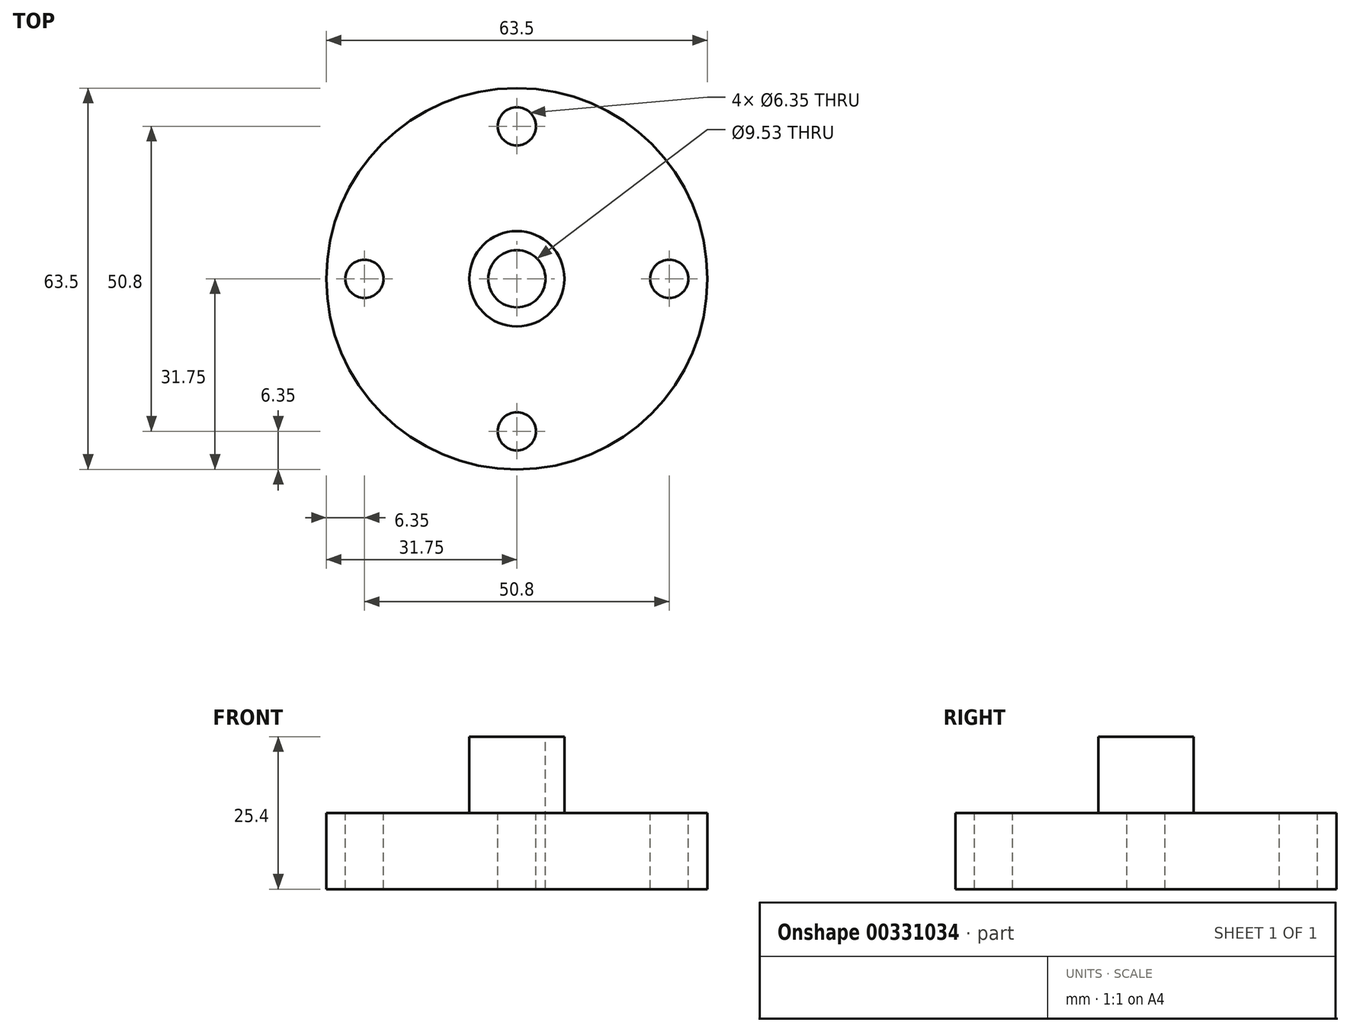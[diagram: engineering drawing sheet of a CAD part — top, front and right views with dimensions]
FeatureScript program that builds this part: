
annotation { "Feature Type Name" : "Feature", "Feature Type Description" : "" }
export const myFeature = defineFeature(function(context is Context, id is Id, definition is map)
    precondition{}
    {
        {
            var Q0;
            Q0=qCreatedBy(makeId("Top.planeOp"),FACE);
            var sketch = newSketch(context, id + "F0", { "sketchPlane" : qUnion([Q0])});
            skCircle(sketch, "E0", {"center": v(0, 0) * mm, "radius": 31.75 * mm});
            skSolve(sketch);
        }
        {
            var Q0;
            Q0=makeQuery(id+"F0.imprint","IMPRINT",FACE,{"disambiguationData":[TD([[makeQuery(id+"F0.imprint","IMPRINT",EDGE,{"derivedFrom":sQuery(id+"F0.wireOp",EDGE,"E0")}),1.0]])]});
            extrude(context, id + "F1", {"entities" : qUnion([Q0]), "depth" : 12.7 * mm});
        }
        {
            var Q0;
            Q0=makeQuery(id+"F1.opExtrude","CAP_FACE",FACE,{"disambiguationData":[OSD([sQuery(id+"F0.wireOp",EDGE,"E0")])],"isStart":false});
            var sketch = newSketch(context, id + "F2", { "sketchPlane" : qUnion([Q0])});
            skCircle(sketch, "E1", {"center": v(0, 0) * mm, "radius": 7.94 * mm});
            skSolve(sketch);
        }
        {
            var Q0;
            Q0=makeQuery(id+"F2.imprint","IMPRINT",FACE,{"disambiguationData":[TD([[makeQuery(id+"F2.imprint","IMPRINT",EDGE,{"derivedFrom":sQuery(id+"F2.wireOp",EDGE,"E1")}),1.0]])]});
            extrude(context, id + "F3", {"entities" : qUnion([Q0]), "operationType" : NewBodyOperationType.ADD, "depth" : 12.7 * mm});
        }
        {
            var Q0;
            Q0=makeQuery(id+"F3.opExtrude","CAP_FACE",FACE,{"disambiguationData":[OSD([sQuery(id+"F2.wireOp",EDGE,"E1")])],"isStart":false});
            var sketch = newSketch(context, id + "F4", { "sketchPlane" : qUnion([Q0])});
            skCircle(sketch, "E2", {"center": v(0, 0) * mm, "radius": 4.76 * mm});
            skSolve(sketch);
        }
        {
            var Q0;
            Q0=makeQuery(id+"F4.imprint","IMPRINT",FACE,{"disambiguationData":[TD([[makeQuery(id+"F4.imprint","IMPRINT",EDGE,{"derivedFrom":sQuery(id+"F4.wireOp",EDGE,"E2")}),1.0]])]});
            extrude(context, id + "F5", {"entities" : qUnion([Q0]), "operationType" : NewBodyOperationType.REMOVE, "oppositeDirection" : true, "depth" : 25.4 * mm});
        }
        {
            var Q0;
            Q0=makeQuery(id+"F1.opExtrude","CAP_FACE",FACE,{"disambiguationData":[OSD([sQuery(id+"F0.wireOp",EDGE,"E0")])],"isStart":false});
            var sketch = newSketch(context, id + "F6", { "sketchPlane" : qUnion([Q0])});
            skCircle(sketch, "E3.0.0", {"center": v(0, 0) * mm, "radius": 31.75 * mm});
            skLineSegment(sketch, "E4", {"start": v(0, 0) * mm, "end": v(25.4, 0) * mm, "construction": true});
            skCircle(sketch, "E5", {"center": v(25.4, 0) * mm, "radius": 3.18 * mm});
            skCircle(sketch, "E6.1.0", {"center": v(0, 25.4) * mm, "radius": 3.18 * mm});
            skCircle(sketch, "E6.2.0", {"center": v(-25.4, 0) * mm, "radius": 3.18 * mm});
            skCircle(sketch, "E6.3.0", {"center": v(0, -25.4) * mm, "radius": 3.18 * mm});
            skSolve(sketch);
        }
        {
            var Q0;
            Q0=makeQuery(id+"F6.imprint","IMPRINT",FACE,{"disambiguationData":[TD([[makeQuery(id+"F6.imprint","IMPRINT",EDGE,{"derivedFrom":sQuery(id+"F6.wireOp",EDGE,"E6.2.0")}),1.0]])]});
            var Q1;
            Q1=makeQuery(id+"F6.imprint","IMPRINT",FACE,{"disambiguationData":[TD([[makeQuery(id+"F6.imprint","IMPRINT",EDGE,{"derivedFrom":sQuery(id+"F6.wireOp",EDGE,"E6.3.0")}),1.0]])]});
            var Q2;
            Q2=makeQuery(id+"F6.imprint","IMPRINT",FACE,{"disambiguationData":[TD([[makeQuery(id+"F6.imprint","IMPRINT",EDGE,{"derivedFrom":sQuery(id+"F6.wireOp",EDGE,"E5")}),1.0]])]});
            var Q3;
            Q3=makeQuery(id+"F6.imprint","IMPRINT",FACE,{"disambiguationData":[TD([[makeQuery(id+"F6.imprint","IMPRINT",EDGE,{"derivedFrom":sQuery(id+"F6.wireOp",EDGE,"E6.1.0")}),1.0]])]});
            extrude(context, id + "F7", {"entities" : qUnion([Q0, Q1, Q2, Q3]), "operationType" : NewBodyOperationType.REMOVE, "oppositeDirection" : true, "depth" : 25.4 * mm});
        }
    });
